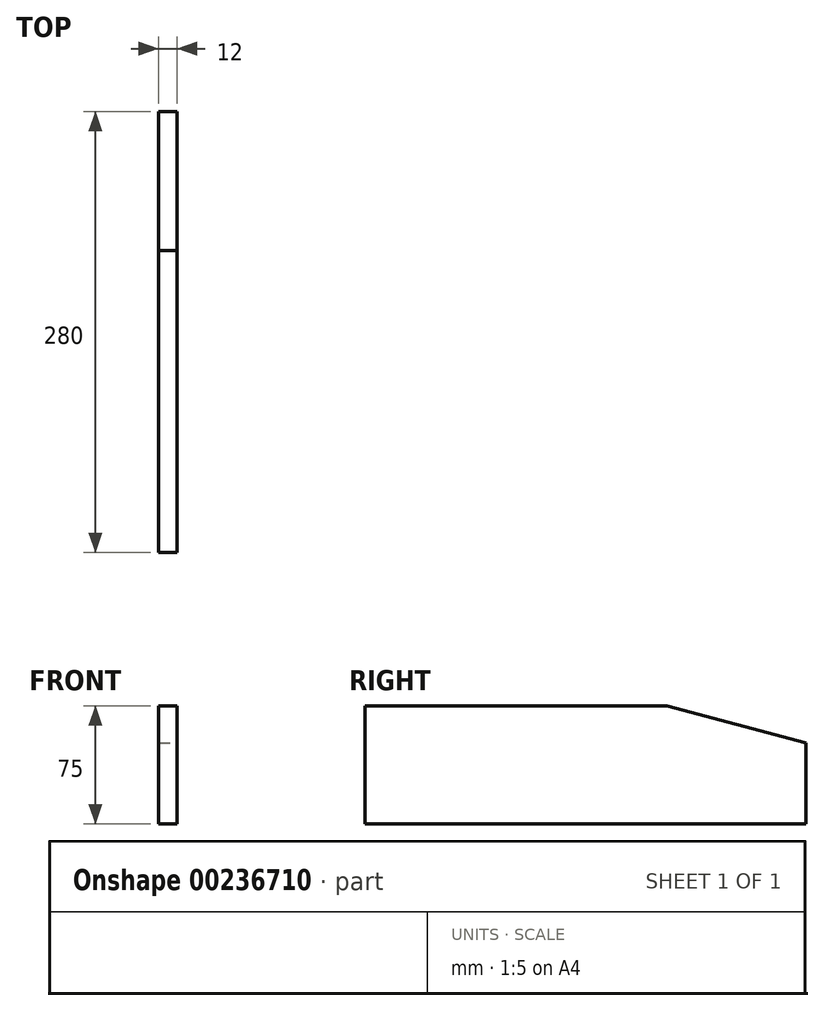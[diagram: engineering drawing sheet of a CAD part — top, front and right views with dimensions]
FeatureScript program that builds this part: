
annotation { "Feature Type Name" : "Feature", "Feature Type Description" : "" }
export const myFeature = defineFeature(function(context is Context, id is Id, definition is map)
    precondition{}
    {
        {
            var Q0;
            Q0=qCreatedBy(makeId("Front.planeOp"),FACE);
            var sketch = newSketch(context, id + "F0", { "sketchPlane" : qUnion([Q0])});
            skLineSegment(sketch, "E0.bottom", {"start": v(0, 0) * mm, "end": v(12, 0) * mm});
            skLineSegment(sketch, "E0.top", {"start": v(0, 75) * mm, "end": v(12, 75) * mm});
            skLineSegment(sketch, "E0.left", {"start": v(0, 0) * mm, "end": v(0, 75) * mm});
            skLineSegment(sketch, "E0.right", {"start": v(12, 0) * mm, "end": v(12, 75) * mm});
            skSolve(sketch);
        }
        {
            var Q0;
            Q0 = qSketchRegion(id + "F0", true);
            extrude(context, id + "F1", {"entities" : qUnion([Q0]), "offsetDistance" : 25 * mm, "depth" : 280 * mm});
        }
        {
            var Q0;
            Q0=makeQuery(id+"F1.opExtrude","SWEPT_FACE",FACE,{"disambiguationData":[OSD([sQuery(id+"F0.wireOp",EDGE,"E0.right")])]});
            var sketch = newSketch(context, id + "F2", { "sketchPlane" : qUnion([Q0])});
            skLineSegment(sketch, "E1", {"start": v(-106.96, 80) * mm, "end": v(5, 50) * mm});
            skLineSegment(sketch, "E2", {"start": v(5, 50) * mm, "end": v(5, 80) * mm});
            skLineSegment(sketch, "E3", {"start": v(5, 80) * mm, "end": v(-106.96, 80) * mm});
            skSolve(sketch);
        }
        {
            var Q0;
            Q0 = qSketchRegion(id + "F2", true);
            extrude(context, id + "F3", {"entities" : qUnion([Q0]), "operationType" : NewBodyOperationType.REMOVE, "endBound" : BoundingType.THROUGH_ALL, "oppositeDirection" : true, "depth" : 25 * mm, "offsetDistance" : 25 * mm});
        }
    });
